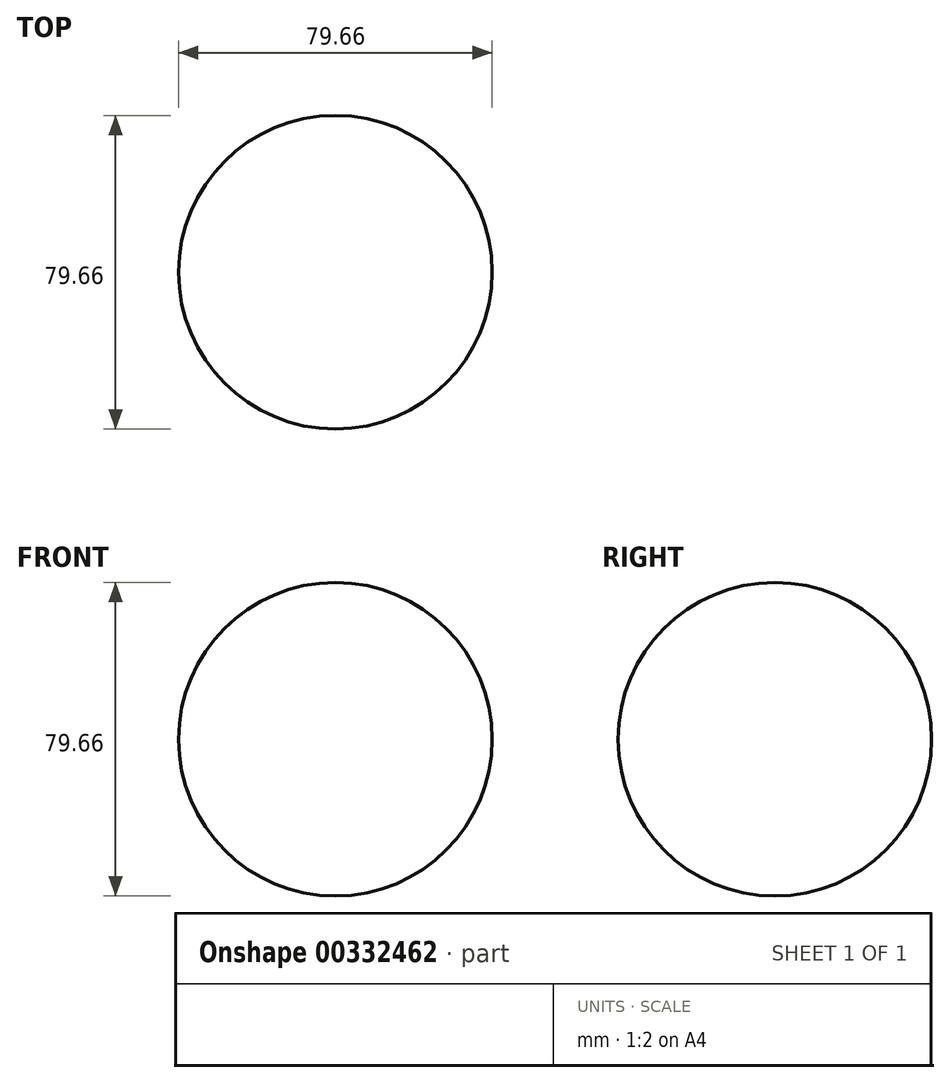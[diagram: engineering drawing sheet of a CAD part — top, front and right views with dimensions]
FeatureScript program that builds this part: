
annotation { "Feature Type Name" : "Feature", "Feature Type Description" : "" }
export const myFeature = defineFeature(function(context is Context, id is Id, definition is map)
    precondition{}
    {
        {
            var Q0;
            Q0=qCreatedBy(makeId("Front.planeOp"),FACE);
            var sketch = newSketch(context, id + "F0", { "sketchPlane" : qUnion([Q0])});
            skCircle(sketch, "E0", {"center": v(0, 0) * mm, "radius": 39.83 * mm});
            skLineSegment(sketch, "E1", {"start": v(0, 60) * mm, "end": v(0, -68.9) * mm});
            skSolve(sketch);
        }
        {
            var Q0;
            {var subQ0=sQuery(id+"F0.wireOp",EDGE,"E1");var subQ1=sQuery(id+"F0.wireOp",EDGE,"E0");var subQ2=makeQuery(id+"F0.imprint","INTERSECT",VERTEX,{"disambiguationData":[OD(0.0)],"derivedFrom":[subQ1,subQ0]});Q0=makeQuery(id+"F0.imprint","IMPRINT",FACE,{"disambiguationData":[TD([[makeQuery(id+"F0.imprint","IMPRINT",EDGE,{"disambiguationData":[TD([[subQ2,1.0]])],"derivedFrom":subQ1}),1.0]])]});}
            var Q1;
            Q1=sQuery(id+"F0.wireOp",EDGE,"E1");
            revolve(context, id + "F1", {"entities" : qUnion([Q0]), "axis" : qUnion([Q1]), "revolveType" : RevolveType.ONE_DIRECTION, "angle" : 360 * degree});
        }
    });
